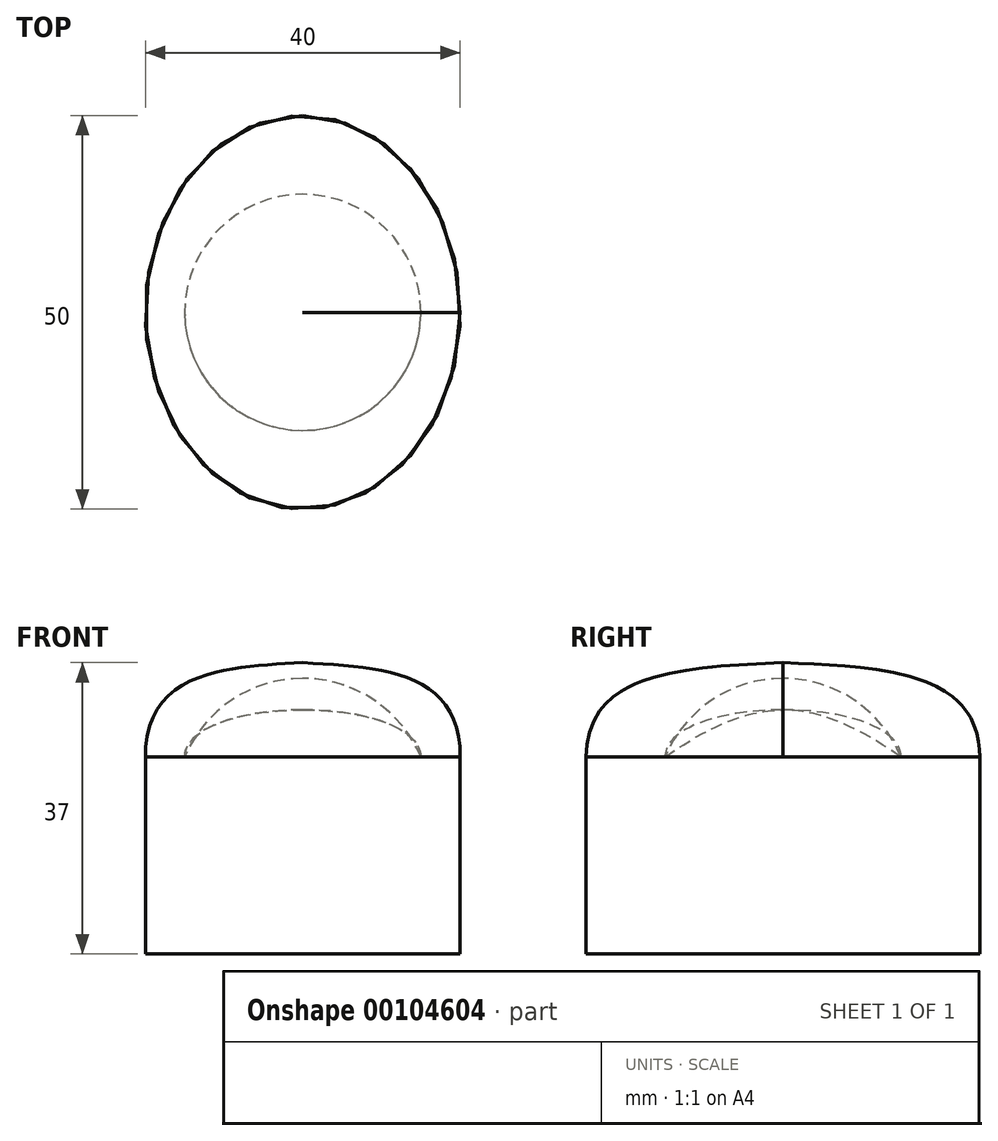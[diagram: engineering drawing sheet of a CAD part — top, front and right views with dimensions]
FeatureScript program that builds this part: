
annotation { "Feature Type Name" : "Feature", "Feature Type Description" : "" }
export const myFeature = defineFeature(function(context is Context, id is Id, definition is map)
    precondition{}
    {
        {
            var Q0;
            Q0=qCreatedBy(makeId("Top.planeOp"),FACE);
            var sketch = newSketch(context, id + "F0", { "sketchPlane" : qUnion([Q0])});
            skLineSegment(sketch, "E0", {"start": v(0, 15) * mm, "end": v(0, -15) * mm});
            skArc(sketch, "E1", {"start": v(0, -15) * mm, "mid": v(15, 0) * mm, "end": v(0, 15) * mm});
            skArc(sketch, "E2", {"start": v(0, 15) * mm, "mid": v(-15, 0) * mm, "end": v(0, -15) * mm});
            skSolve(sketch);
        }
        {
            var Q0;
            Q0=qCreatedBy(makeId("Right.planeOp"),FACE);
            var sketch = newSketch(context, id + "F1", { "sketchPlane" : qUnion([Q0])});
            skLineSegment(sketch, "E3", {"start": v(0, 0) * mm, "end": v(0, 10) * mm});
            skArc(sketch, "E4", {"start": v(15, 0) * mm, "mid": v(0, 10) * mm, "end": v(-15, 0) * mm});
            skSolve(sketch);
        }
        {
            var Q0;
            Q0=qCreatedBy(makeId("Front.planeOp"),FACE);
            var sketch = newSketch(context, id + "F2", { "sketchPlane" : qUnion([Q0])});
            skFitSpline(sketch, "E5", {"points": [v(0, 10) * mm, v(15, 0) * mm], "startDerivative": vector(30, 0) * mm, "endDerivative": vector(0, -15) * mm});
            skLineSegment(sketch, "E6", {"start": v(15, 0) * mm, "end": v(15, -6.42) * mm, "construction": true});
            skLineSegment(sketch, "E7", {"start": v(0, 10) * mm, "end": v(-5.92, 10) * mm, "construction": true});
            skSolve(sketch);
        }
        {
            var Q0;
            Q0=sQuery(id+"F0.wireOp",EDGE,"E1");
            var Q1;
            Q1=sQuery(id+"F1.wireOp",EDGE,"E4");
            var Q2;
            Q2=sQuery(id+"F2.wireOp",EDGE,"E5");
            loft(context, id + "F3", {"bodyType" : ToolBodyType.SURFACE, "wireProfilesArray" : [{ "wireProfileEntities" : qUnion([Q0]) }, { "wireProfileEntities" : qUnion([Q1]) }], "guidesArray" : [{ "guideEntities" : qUnion([Q2]), "guideDerivativeType" : LoftGuideDerivativeType.DEFAULT, "guideDerivativeMagnitude" : 1 }]});
        }
        {
            var Q0;
            Q0=makeQuery(id+"F0.imprint","IMPRINT",FACE,{"disambiguationData":[TD([[makeQuery(id+"F0.imprint","IMPRINT",EDGE,{"derivedFrom":sQuery(id+"F0.wireOp",EDGE,"E0")}),1.0]])]});
            var Q1;
            Q1=makeQuery(id+"F3.opLoft","SWEPT_FACE",FACE,{"disambiguationData":[OSD([sQuery(id+"F0.wireOp",VERTEX,"E1.start"),sQuery(id+"F0.wireOp",VERTEX,"E1.end"),sQuery(id+"F0.wireOp",EDGE,"E1"),sQuery(id+"F1.wireOp",VERTEX,"E4.start"),sQuery(id+"F1.wireOp",VERTEX,"E4.end"),sQuery(id+"F1.wireOp",EDGE,"E4")])]});
            extrude(context, id + "F4", {"entities" : qUnion([Q0]), "endBound" : BoundingType.UP_TO_SURFACE, "endBoundEntityFace" : qUnion([Q1]), "depth" : 25 * mm});
        }
        {
            var Q0;
            Q0=makeQuery(id+"F4.opExtrude","SWEPT_BODY",BODY,{"disambiguationData":[OSD([sQuery(id+"F0.wireOp",EDGE,"E0"),sQuery(id+"F0.wireOp",EDGE,"E1")])]});
            var Q1;
            Q1=makeQuery(id+"F4.opExtrude","SWEPT_FACE",FACE,{"disambiguationData":[OSD([sQuery(id+"F0.wireOp",EDGE,"E0")])]});
            mirror(context, id + "F5", {"operationType" : NewBodyOperationType.ADD, "entities" : qUnion([Q0]), "mirrorPlane" : qUnion([Q1])});
        }
        {
            var Q0;
            Q0=qCreatedBy(makeId("Top.planeOp"),FACE);
            var sketch = newSketch(context, id + "F6", { "sketchPlane" : qUnion([Q0])});
            skCircle(sketch, "E8", {"center": v(0, 0) * mm, "radius": 15 * mm});
            skSolve(sketch);
        }
        {
            var Q0;
            Q0=qCreatedBy(makeId("Front.planeOp"),FACE);
            var sketch = newSketch(context, id + "F7", { "sketchPlane" : qUnion([Q0])});
            skLineSegment(sketch, "E9", {"start": v(15, 0) * mm, "end": v(0, 0) * mm});
            skLineSegment(sketch, "E10", {"start": v(0, 0) * mm, "end": v(0, 6) * mm});
            skFitSpline(sketch, "E11", {"points": [v(0, 6) * mm, v(15, 0) * mm], "startDerivative": vector(25.5, 0) * mm, "endDerivative": vector(0, -10.5) * mm});
            skLineSegment(sketch, "E12", {"start": v(0, 6) * mm, "end": v(-5, 6) * mm});
            skLineSegment(sketch, "E13", {"start": v(15, 0) * mm, "end": v(15, -4.54) * mm});
            skFitSpline(sketch, "E14.MirrorCS", {"points": [v(0, 6) * mm, v(-15, 0) * mm], "startDerivative": vector(-25.5, 0) * mm, "endDerivative": vector(0, -10.5) * mm});
            skSolve(sketch);
        }
        {
            var Q0;
            Q0=makeQuery(id+"F6.imprint","IMPRINT",FACE,{"disambiguationData":[TD([[makeQuery(id+"F6.imprint","IMPRINT",EDGE,{"derivedFrom":sQuery(id+"F6.wireOp",EDGE,"E8")}),1.0]])]});
            var Q1;
            Q1=sQuery(id+"F7.wireOp",VERTEX,"E11.0.internal");
            var Q2;
            Q2=sQuery(id+"F7.wireOp",EDGE,"E11");
            var Q3;
            Q3=sQuery(id+"F7.wireOp",EDGE,"E14.MirrorCS");
            loft(context, id + "F8", {"addGuides" : true, "sheetProfilesArray" : [{ "sheetProfileEntities" : qUnion([Q0]) }, { "sheetProfileEntities" : qUnion([Q1]) }], "guidesArray" : [{ "guideEntities" : qUnion([Q2]), "guideDerivativeType" : LoftGuideDerivativeType.DEFAULT, "guideDerivativeMagnitude" : 1 }, { "guideEntities" : qUnion([Q3]), "guideDerivativeType" : LoftGuideDerivativeType.DEFAULT, "guideDerivativeMagnitude" : 1 }]});
        }
        {
            var Q0;
            Q0=makeQuery(id+"F7.imprint","IMPRINT",FACE,{"disambiguationData":[TD([[makeQuery(id+"F7.imprint","IMPRINT",EDGE,{"derivedFrom":sQuery(id+"F7.wireOp",EDGE,"E9")}),-1.0]])]});
            var Q1;
            Q1=sQuery(id+"F7.wireOp",EDGE,"E10");
            revolve(context, id + "F9", {"entities" : qUnion([Q0]), "axis" : qUnion([Q1]), "revolveType" : RevolveType.FULL});
        }
        {
            var Q0;
            Q0=qCreatedBy(makeId("Top.planeOp"),FACE);
            var sketch = newSketch(context, id + "F10", { "sketchPlane" : qUnion([Q0])});
            skEllipse(sketch, "E15", {"center": v(0, 0) * mm, "majorRadius": 25 * mm, "minorRadius": 20 * mm, "majorAxis": v(0, 1)});
            skLineSegment(sketch, "E16", {"start": v(0, 25) * mm, "end": v(0, 0) * mm, "construction": true});
            skLineSegment(sketch, "E17", {"start": v(20, 0) * mm, "end": v(0, 0) * mm, "construction": true});
            skSolve(sketch);
        }
        {
            var Q0;
            Q0=makeQuery(id+"F10.imprint","IMPRINT",FACE,{"disambiguationData":[TD([[makeQuery(id+"F10.imprint","IMPRINT",EDGE,{"derivedFrom":sQuery(id+"F10.wireOp",EDGE,"E15")}),1.0]])]});
            extrude(context, id + "F11", {"entities" : qUnion([Q0]), "oppositeDirection" : true, "depth" : 25 * mm});
        }
        {
            var Q0;
            Q0=qCreatedBy(makeId("Front.planeOp"),FACE);
            var sketch = newSketch(context, id + "F12", { "sketchPlane" : qUnion([Q0])});
            skLineSegment(sketch, "E18", {"start": v(0, 0) * mm, "end": v(0, 12) * mm});
            skSolve(sketch);
        }
        {
            var Q0;
            Q0=makeQuery(id+"F11.opExtrude","CAP_FACE",FACE,{"disambiguationData":[OSD([sQuery(id+"F10.wireOp",EDGE,"E15")])],"isStart":true});
            var Q1;
            Q1=sQuery(id+"F12.wireOp",VERTEX,"E18.end");
            var Q2;
            Q2=sQuery(id+"F12.wireOp",VERTEX,"E18.end");
            loft(context, id + "F13", {"startCondition" : LoftEndDerivativeType.MATCH_TANGENT, "startMagnitude" : 2.5, "sheetProfilesArray" : [{ "sheetProfileEntities" : qUnion([Q0]) }, { "sheetProfileEntities" : qUnion([Q1]) }], "connections" : [{ "connectionEntities" : qUnion([Q2]), "connectionEdgeQueries" : qUnion([]), "connectionEdgeParameters" : [] }]});
        }
    });
